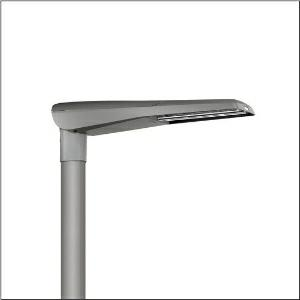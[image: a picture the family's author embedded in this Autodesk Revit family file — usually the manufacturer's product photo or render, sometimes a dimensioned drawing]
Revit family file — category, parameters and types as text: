
# Revit family: streetlight_sl_11_iq_mini___st1_2a_5xc2ac1f08ge_c732
name_source: partatom
category: Lighting Fixtures
units: mm (PartAtom-declared; Revit-internal decimal feet)

## family parameters
Cut with Voids When Loaded = No
Host = Face
Light Source = No
Part Type = Normal
Room Calculation Point = No
Round Connector Dimension = Use Diameter
Shared = No

## types (1)
- --- (1 x LED, 3040 lm, 25.3 W, 2200K)
    Apparent Load = 25 VA
    CIE Flux Codes = 32 70 96 100 100
    Color Rendering = 70
    Color Temperature = 2200K
    Default Elevation = 1800 mm
    Description = Streetlight SL 11 iQ mini, mast luminaire, primary light control with 3 zone facetted reflector, of plastic, silver coated, highly specular, primary optical cover: cover, of PMMA, transparent, light distribution: ST1.2a, light emission: direct distribution, primary light characteristic: asymmetric, installation type: post-top, side-entry, lamps: LED, High Power LED, rated values: 3.570lm | 24,9W | 143,4lm/W (begin service life); end service life: 3.570lm | 25,7W; at 50% lumin. flux: 1.785lm | 12,8W | 139,5lm/W, colour temperature: 2200/2700/3000/4000K, colour rendering: CRI > 70, light colour: 722/727/730/740, light setting 1 begin service life: 100% | 3.570lm | 24,9W | 143,4lm/W | 3.000K, light setting 1 end service life: 25,7W, further light settings possible, control: Street-Remote, Auto-Match, Temp-Guard, Lumen-Switch, Night-Set, Smart-Wire, Light-Fading, Desk-Remote (wireless, voltage-free reading and setting of iQ features in the workshop via application-optimized NFC function/RFID function), optimised constant luminous flux control (CLO 2.0), with cable H07RN-F 3x 1.5mm², mains connection: 230..240V, AC, 50/60Hz, connection cable pre-assembled, cable length: 6,5m, luminaire housing, of diecast aluminium, powder-coated, SITECO metallic grey (DB 702S), please order mast flange separately, inclination adjustable without tools: 0°, 5°, 10°, 15° (post-top) | 0°, -5°, -10°, -15° (side-entry), sealing non-destructively replaceable, multi-level sealing system, length: 736mm, width: 174mm, height: 116mm, mast flange for spigot size: 42mm (side-entry): 5XC10008XM4, 60/48mm (side-entry/post-top): 5XC10108XM2, 76/60mm (side-entry/post-top): 5XC10108XM1, equipment: standard, protection rating (complete): IP66, insulation class (complete): insulation class II (safety insulation), certification: CE, ENEC, ENEC+, VDE, impact resistance: IK10, permissible operating ambient temperature for outdoor applications: -25..+50°C, standard-compliant lighting for roads and squares, Environmental Product Declaration (EPD) tested and certified by an independent institute, packaging unit: 1 piece

Light Distribution: ST1.2a
    Height = 116 mm
    Lamp = 1 x LED
    Lamp Light Flux = 3040 lm
    Lamp Power = 25.3 W
    Lamp count = 1
    Length = 736 mm
    Luminous efficacy = 120 lm/W
    Manufacturer = Siteco
    ModVariant = No
    Model = 5XC2AC1F08GE
    Number of Poles = 1
    OnlyDefault = Yes
    Power Factor = 1
    Product Name = Streetlight SL 11 iQ mini | ST1.2a
    Product group = mast luminaire | pylon top
    ProductGroupID = 6100
    Protection Class = Protection class II
    Protection Degree = IP 66
    RLX_Detail_Level = 1
    RLX_Emergency_Light_Flux = 0 lm
    RLX_Emergency_Type = 0
    RLX_Emergency_Type_DB = No
    RlxData = <blob elided: 53689 chars, md5=2f301029>
    Socket = socket
    Standby Power = 0 W
    System Light Flux = 3040 lm
    System Power = 25 W
    Type Comments = individual setting: luminous flux: 100 % | dim-lin: 254 | 351 mA
    Type Image = l_1003508.jpg
    URL = http://relux.com
    VarID = @adj_042155
    Voltage = 0 V
    Weight = 0.00 kg
    Width = 174 mm

## geometry (parser evidence)
native form markers: Blend x4, Sweep x10
no freeform markers — native parametric forms only
